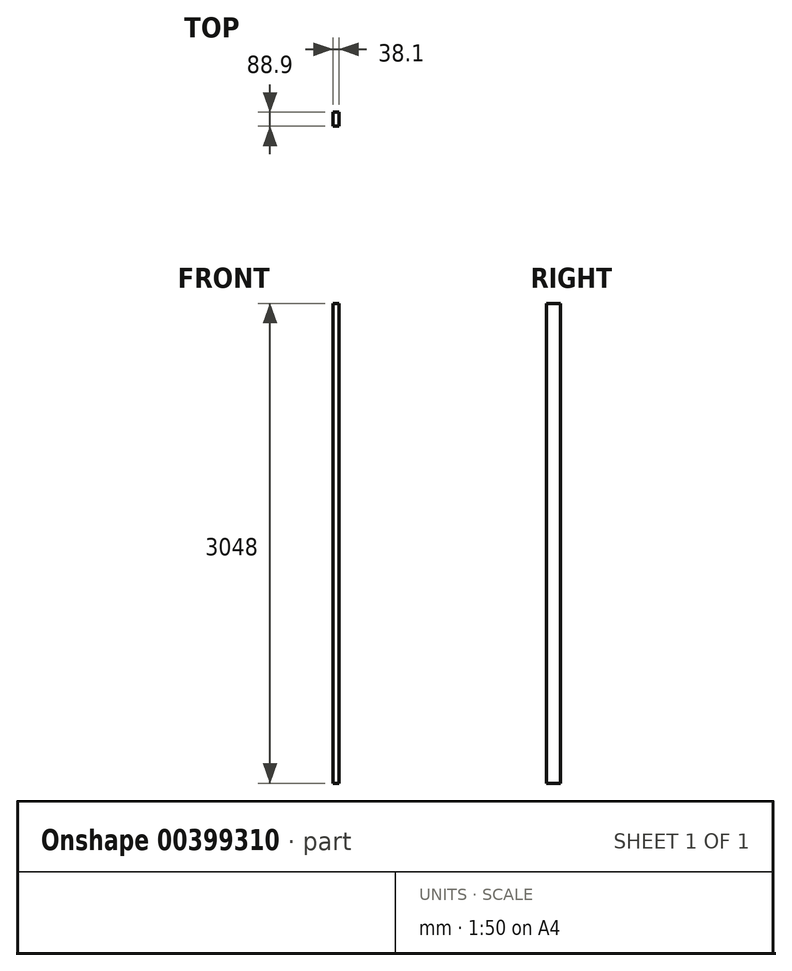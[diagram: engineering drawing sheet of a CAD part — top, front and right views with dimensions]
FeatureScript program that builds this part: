
annotation { "Feature Type Name" : "Feature", "Feature Type Description" : "" }
export const myFeature = defineFeature(function(context is Context, id is Id, definition is map)
    precondition{}
    {
        {
            var Q0;
            Q0=qCreatedBy(makeId("Front.planeOp"),FACE);
            var sketch = newSketch(context, id + "F0", { "sketchPlane" : qUnion([Q0])});
            skLineSegment(sketch, "E0.bottom", {"start": v(19.05, -1524) * mm, "end": v(-19.05, -1524) * mm});
            skLineSegment(sketch, "E0.top", {"start": v(19.05, 1524) * mm, "end": v(-19.05, 1524) * mm});
            skLineSegment(sketch, "E0.left", {"start": v(19.05, -1524) * mm, "end": v(19.05, 1524) * mm});
            skLineSegment(sketch, "E0.right", {"start": v(-19.05, -1524) * mm, "end": v(-19.05, 1524) * mm});
            skPoint(sketch, "E0.middle", {"position": v(0, 0) * mm});
            skSolve(sketch);
        }
        {
            var Q0;
            Q0 = qSketchRegion(id + "F0", true);
            extrude(context, id + "F1", {"entities" : qUnion([Q0]), "depth" : 88.9 * mm});
        }
    });
